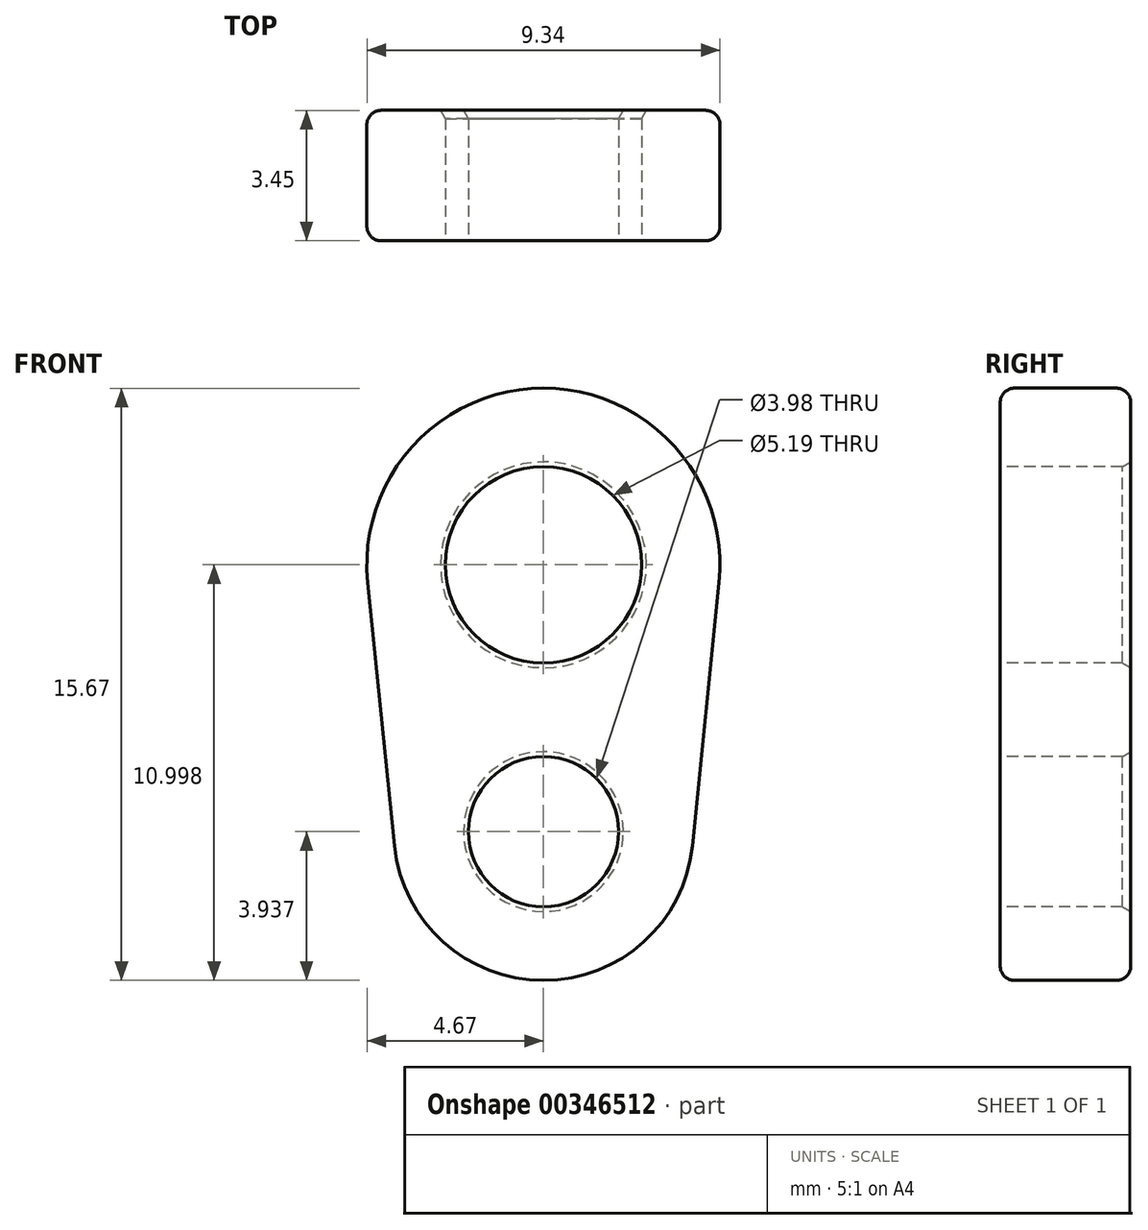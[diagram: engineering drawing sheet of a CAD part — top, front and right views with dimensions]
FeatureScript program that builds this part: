
annotation { "Feature Type Name" : "Feature", "Feature Type Description" : "" }
export const myFeature = defineFeature(function(context is Context, id is Id, definition is map)
    precondition{}
    {
        {
            var Q0;
            Q0=qCreatedBy(makeId("Front.planeOp"),FACE);
            var sketch = newSketch(context, id + "F0", { "sketchPlane" : qUnion([Q0])});
            skLineSegment(sketch, "E0", {"start": v(0, 3.52) * mm, "end": v(0, -3.52) * mm, "construction": true});
            skArc(sketch, "E1", {"start": v(4.65, 3.05) * mm, "mid": v(0, 8.2) * mm, "end": v(-4.65, 3.05) * mm});
            skArc(sketch, "E2", {"start": v(3.94, -3.92) * mm, "mid": v(0, -7.48) * mm, "end": v(-3.94, -3.92) * mm});
            skLineSegment(sketch, "E3", {"start": v(-4.65, 3.05) * mm, "end": v(-3.94, -3.92) * mm});
            skLineSegment(sketch, "E4", {"start": v(4.65, 3.05) * mm, "end": v(3.94, -3.92) * mm});
            skSolve(sketch);
        }
        {
            var Q0;
            Q0=makeQuery(id+"F0.imprint","IMPRINT",FACE,{"disambiguationData":[TD([[makeQuery(id+"F0.imprint","IMPRINT",EDGE,{"derivedFrom":sQuery(id+"F0.wireOp",EDGE,"E1")}),1.0]])]});
            extrude(context, id + "F1", {"entities" : qUnion([Q0]), "oppositeDirection" : true, "depth" : 3.45 * mm});
        }
        {
            var Q0;
            Q0=makeQuery(id+"F1.opExtrude","CAP_FACE",FACE,{"disambiguationData":[OSD([sQuery(id+"F0.wireOp",EDGE,"E1"),sQuery(id+"F0.wireOp",EDGE,"E2"),sQuery(id+"F0.wireOp",EDGE,"E3"),sQuery(id+"F0.wireOp",EDGE,"E4")])],"isStart":true});
            var sketch = newSketch(context, id + "F2", { "sketchPlane" : qUnion([Q0])});
            skCircle(sketch, "E5", {"center": v(0, 3.52) * mm, "radius": 2.6 * mm});
            skLineSegment(sketch, "E6", {"start": v(0, 3.52) * mm, "end": v(0, -3.54) * mm, "construction": true});
            skCircle(sketch, "E7", {"center": v(0, -3.54) * mm, "radius": 1.99 * mm});
            skSolve(sketch);
        }
        {
            var Q0;
            Q0=qSketchRegion(id+"F2",true);
            extrude(context, id + "F3", {"entities" : qUnion([Q0]), "operationType" : NewBodyOperationType.REMOVE, "endBound" : BoundingType.THROUGH_ALL, "oppositeDirection" : true, "depth" : 25.4 * mm});
        }
        {
            var Q0;
            Q0=makeQuery(id+"F3.boolean.opBoolean","COPY",EDGE,{"derivedFrom":makeQuery(id+"F3.opExtrude","CAP_EDGE",EDGE,{"disambiguationData":[OSD([sQuery(id+"F2.wireOp",EDGE,"E5")])],"isStart":true})});
            var Q1;
            Q1=makeQuery(id+"F3.boolean.opBoolean","COPY",EDGE,{"derivedFrom":makeQuery(id+"F3.opExtrude","CAP_EDGE",EDGE,{"disambiguationData":[OSD([sQuery(id+"F2.wireOp",EDGE,"E7")])],"isStart":true})});
            var Q2;
            Q2=makeQuery(id+"F3.boolean.opBoolean","INTERSECT",EDGE,{"derivedFrom":[makeQuery(id+"F1.opExtrude","CAP_FACE",FACE,{"disambiguationData":[OSD([sQuery(id+"F0.wireOp",EDGE,"E1"),sQuery(id+"F0.wireOp",EDGE,"E2"),sQuery(id+"F0.wireOp",EDGE,"E3"),sQuery(id+"F0.wireOp",EDGE,"E4")])],"isStart":false}),makeQuery(id+"F3.opExtrude","SWEPT_FACE",FACE,{"disambiguationData":[OSD([sQuery(id+"F2.wireOp",EDGE,"E7")])]})]});
            var Q3;
            Q3=makeQuery(id+"F3.boolean.opBoolean","INTERSECT",EDGE,{"derivedFrom":[makeQuery(id+"F1.opExtrude","CAP_FACE",FACE,{"disambiguationData":[OSD([sQuery(id+"F0.wireOp",EDGE,"E1"),sQuery(id+"F0.wireOp",EDGE,"E2"),sQuery(id+"F0.wireOp",EDGE,"E3"),sQuery(id+"F0.wireOp",EDGE,"E4")])],"isStart":false}),makeQuery(id+"F3.opExtrude","SWEPT_FACE",FACE,{"disambiguationData":[OSD([sQuery(id+"F2.wireOp",EDGE,"E5")])]})]});
            chamfer(context, id + "F4", {"entities" : qUnion([Q0, Q1, Q2, Q3]), "chamferType" : ChamferType.OFFSET_ANGLE, "width" : 0.13 * mm, "oppositeDirection" : false, "angle" : 60 * degree, "tangentPropagation" : true});
        }
        {
            var Q0;
            Q0=makeQuery(id+"F1.opExtrude","CAP_EDGE",EDGE,{"disambiguationData":[OSD([sQuery(id+"F0.wireOp",EDGE,"E2")])],"isStart":true});
            var Q1;
            Q1=makeQuery(id+"F1.opExtrude","CAP_EDGE",EDGE,{"disambiguationData":[OSD([sQuery(id+"F0.wireOp",EDGE,"E2")])],"isStart":false});
            fillet(context, id + "F5", {"entities" : qUnion([Q0, Q1]), "radius" : 0.38 * mm, "tangentPropagation" : true, "allowEdgeOverflow" : false});
        }
    });
